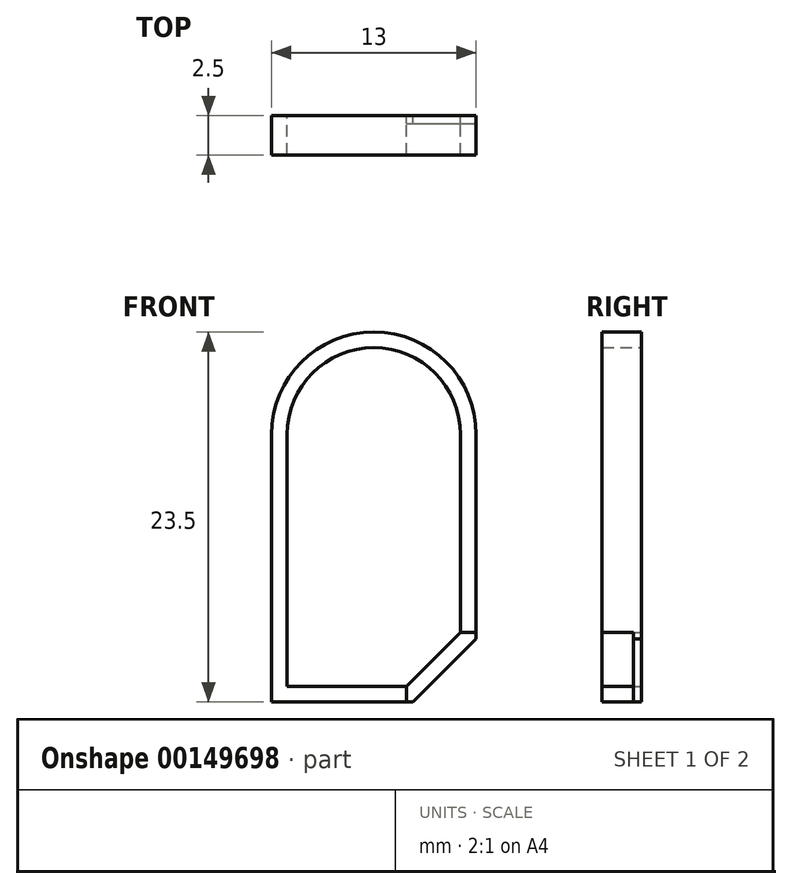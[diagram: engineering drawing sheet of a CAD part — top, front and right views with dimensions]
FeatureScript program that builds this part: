
annotation { "Feature Type Name" : "Feature", "Feature Type Description" : "" }
export const myFeature = defineFeature(function(context is Context, id is Id, definition is map)
    precondition{}
    {
        {
            var Q0;
            Q0=qCreatedBy(makeId("Front.planeOp"),FACE);
            var sketch = newSketch(context, id + "F0", { "sketchPlane" : qUnion([Q0])});
            skArc(sketch, "E0", {"start": v(6.5, 0) * mm, "mid": v(0, 6.5) * mm, "end": v(-6.5, 0) * mm});
            skLineSegment(sketch, "E1", {"start": v(-6.5, 0) * mm, "end": v(-6.5, -17) * mm});
            skLineSegment(sketch, "E2", {"start": v(2.5, -17) * mm, "end": v(6.5, -13) * mm});
            skLineSegment(sketch, "E3", {"start": v(6.5, -13) * mm, "end": v(6.5, 0) * mm});
            skLineSegment(sketch, "E4", {"start": v(-6.5, -17) * mm, "end": v(2.5, -17) * mm});
            skLineSegment(sketch, "E5.0", {"start": v(-5.5, 0) * mm, "end": v(-5.5, -16) * mm});
            skArc(sketch, "E5.1", {"start": v(5.5, 0) * mm, "mid": v(0, 5.5) * mm, "end": v(-5.5, 0) * mm});
            skLineSegment(sketch, "E5.2", {"start": v(-5.5, -16) * mm, "end": v(2.09, -16) * mm});
            skLineSegment(sketch, "E5.3", {"start": v(2.09, -16) * mm, "end": v(5.5, -12.59) * mm});
            skLineSegment(sketch, "E5.4", {"start": v(5.5, -12.59) * mm, "end": v(5.5, 0) * mm});
            skPoint(sketch, "E6", {"position": v(6.5, -17) * mm});
            skSolve(sketch);
        }
        {
            var Q0;
            Q0 = qSketchRegion(id + "F0", true);
            extrude(context, id + "F1", {"entities" : qUnion([Q0]), "depth" : 2.5 * mm});
        }
        {
            var Q0;
            Q0=makeQuery(id+"F1.opExtrude","CAP_FACE",FACE,{"disambiguationData":[OSD([sQuery(id+"F0.wireOp",EDGE,"E0"),sQuery(id+"F0.wireOp",EDGE,"E1"),sQuery(id+"F0.wireOp",EDGE,"E2"),sQuery(id+"F0.wireOp",EDGE,"E3"),sQuery(id+"F0.wireOp",EDGE,"E4"),sQuery(id+"F0.wireOp",EDGE,"E5.0"),sQuery(id+"F0.wireOp",EDGE,"E5.1"),sQuery(id+"F0.wireOp",EDGE,"E5.2"),sQuery(id+"F0.wireOp",EDGE,"E5.3"),sQuery(id+"F0.wireOp",EDGE,"E5.4")])],"isStart":false});
            var sketch = newSketch(context, id + "F2", { "sketchPlane" : qUnion([Q0])});
            skLineSegment(sketch, "E7", {"start": v(5.5, -12.59) * mm, "end": v(6.5, -12.59) * mm});
            skLineSegment(sketch, "E8", {"start": v(6.5, -12.59) * mm, "end": v(6.5, -13) * mm});
            skLineSegment(sketch, "E9", {"start": v(2.09, -16) * mm, "end": v(2.09, -17) * mm});
            skLineSegment(sketch, "E10", {"start": v(2.09, -17) * mm, "end": v(2.5, -17) * mm});
            skLineSegment(sketch, "E11", {"start": v(2.5, -17) * mm, "end": v(6.5, -13) * mm});
            skLineSegment(sketch, "E12", {"start": v(5.5, -12.59) * mm, "end": v(2.09, -16) * mm});
            skSolve(sketch);
        }
        {
            var Q0;
            Q0=makeQuery(id+"F2.imprint","IMPRINT",FACE,{"disambiguationData":[TD([[makeQuery(id+"F2.imprint","IMPRINT",EDGE,{"derivedFrom":sQuery(id+"F2.wireOp",EDGE,"E7")}),-1.0]])]});
            extrude(context, id + "F3", {"entities" : qUnion([Q0]), "operationType" : NewBodyOperationType.REMOVE, "oppositeDirection" : true, "depth" : 2 * mm});
        }
    });
